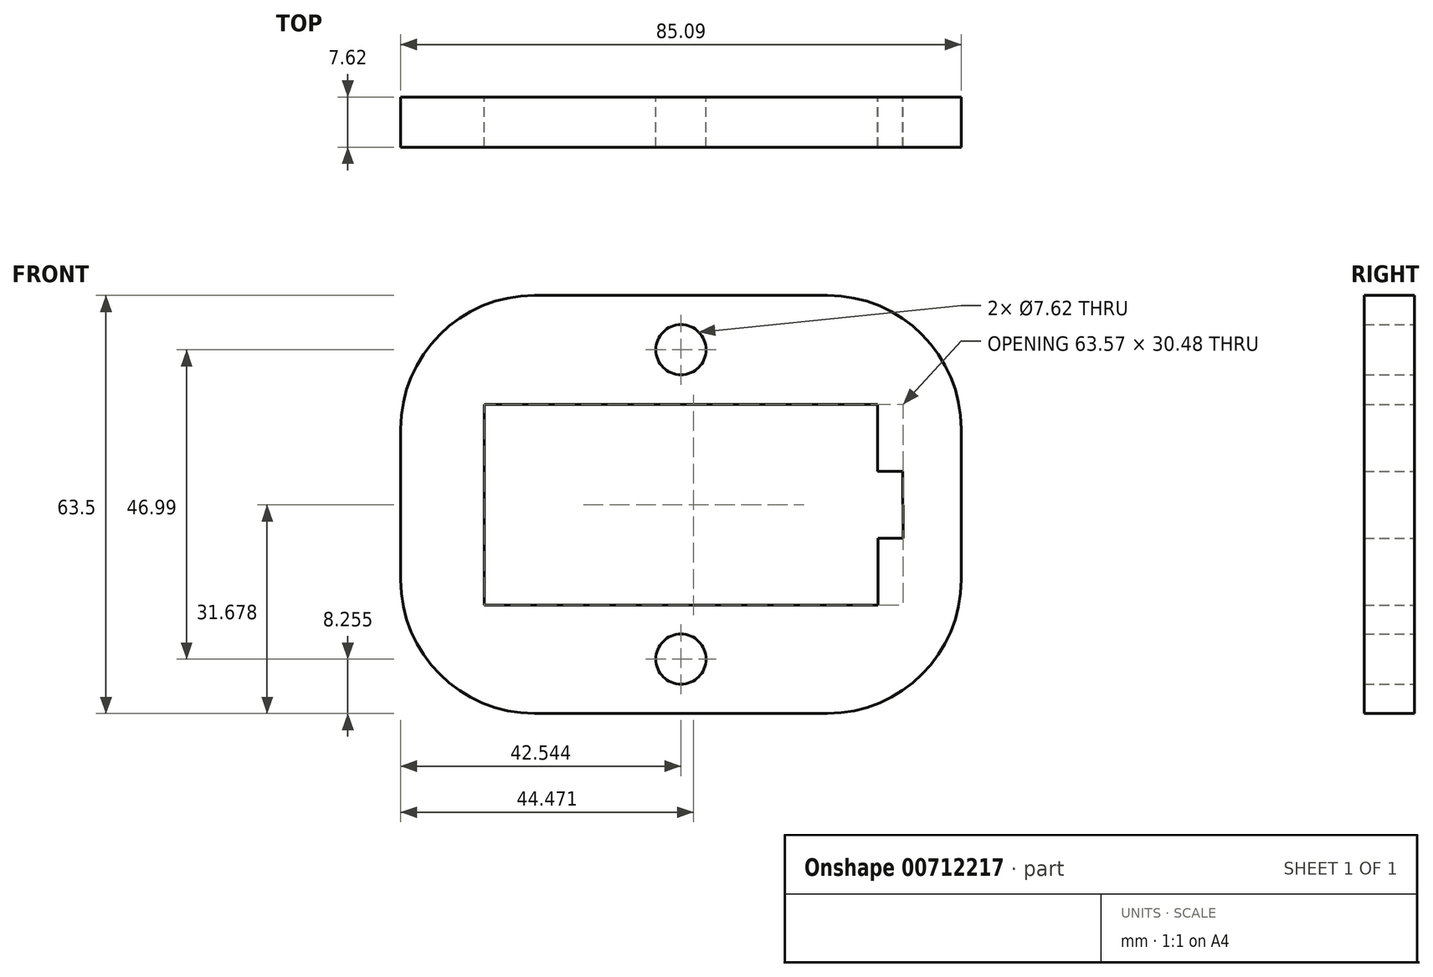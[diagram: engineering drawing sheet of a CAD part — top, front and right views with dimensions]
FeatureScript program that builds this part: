
annotation { "Feature Type Name" : "Feature", "Feature Type Description" : "" }
export const myFeature = defineFeature(function(context is Context, id is Id, definition is map)
    precondition{}
    {
        {
            var Q0;
            Q0=qCreatedBy(makeId("Front.planeOp"),FACE);
            var sketch = newSketch(context, id + "F0", { "sketchPlane" : qUnion([Q0])});
            skLineSegment(sketch, "E0", {"start": v(-66.05, 20.3) * mm, "end": v(19.04, 20.3) * mm});
            skLineSegment(sketch, "E1", {"start": v(19.04, 20.3) * mm, "end": v(19.04, 83.8) * mm});
            skLineSegment(sketch, "E2", {"start": v(19.04, 83.8) * mm, "end": v(-66.05, 83.8) * mm});
            skLineSegment(sketch, "E3", {"start": v(-66.05, 83.8) * mm, "end": v(-66.05, 20.3) * mm});
            skLineSegment(sketch, "E4", {"start": v(-42.14, 36.73) * mm, "end": v(-53.36, 36.73) * mm});
            skLineSegment(sketch, "E5", {"start": v(-42.14, 67.2) * mm, "end": v(-53.36, 67.2) * mm});
            skLineSegment(sketch, "E6", {"start": v(-53.36, 67.2) * mm, "end": v(-53.36, 36.73) * mm});
            skLineSegment(sketch, "E7", {"start": v(-53.36, 36.73) * mm, "end": v(6.34, 36.73) * mm});
            skLineSegment(sketch, "E8", {"start": v(6.34, 67.2) * mm, "end": v(-42.14, 67.2) * mm});
            skCircle(sketch, "E9", {"center": v(-23.5, 75.54) * mm, "radius": 3.81 * mm});
            skCircle(sketch, "E10", {"center": v(-23.5, 28.55) * mm, "radius": 3.81 * mm});
            skLineSegment(sketch, "E11", {"start": v(6.34, 67.2) * mm, "end": v(6.34, 57.05) * mm});
            skLineSegment(sketch, "E12", {"start": v(6.4, 36.74) * mm, "end": v(6.4, 46.9) * mm});
            skLineSegment(sketch, "E13", {"start": v(6.4, 46.9) * mm, "end": v(10.2, 46.9) * mm});
            skLineSegment(sketch, "E14", {"start": v(6.34, 57.05) * mm, "end": v(10.15, 57.05) * mm});
            skLineSegment(sketch, "E15", {"start": v(10.15, 57.05) * mm, "end": v(10.2, 46.9) * mm});
            skLineSegment(sketch, "E16", {"start": v(-53.36, 67.2) * mm, "end": v(6.34, 67.2) * mm});
            skLineSegment(sketch, "E17", {"start": v(10.2, 46.9) * mm, "end": v(6.4, 46.9) * mm});
            skLineSegment(sketch, "E18", {"start": v(6.4, 36.74) * mm, "end": v(-53.36, 36.73) * mm});
            skLineSegment(sketch, "E19", {"start": v(-53.36, 36.73) * mm, "end": v(-53.36, 67.2) * mm});
            skSolve(sketch);
        }
        {
            var Q0;
            Q0=makeQuery(id+"F0.imprint","IMPRINT",FACE,{"disambiguationData":[TD([[makeQuery(id+"F0.imprint","IMPRINT",EDGE,{"derivedFrom":sQuery(id+"F0.wireOp",EDGE,"E0")}),1.0]])]});
            extrude(context, id + "F1", {"entities" : qUnion([Q0]), "depth" : 7.62 * mm, "offsetDistance" : 25.4 * mm});
        }
        {
            var Q0;
            Q0=makeQuery(id+"F1.opExtrude","SWEPT_EDGE",EDGE,{"disambiguationData":[OSD([sQuery(id+"F0.wireOp",EDGE,"E2"),sQuery(id+"F0.wireOp",EDGE,"E3")])]});
            var Q1;
            Q1=makeQuery(id+"F1.opExtrude","SWEPT_EDGE",EDGE,{"disambiguationData":[OSD([sQuery(id+"F0.wireOp",EDGE,"E0"),sQuery(id+"F0.wireOp",EDGE,"E3")])]});
            var Q2;
            Q2=makeQuery(id+"F1.opExtrude","SWEPT_EDGE",EDGE,{"disambiguationData":[OSD([sQuery(id+"F0.wireOp",EDGE,"E0"),sQuery(id+"F0.wireOp",EDGE,"E1")])]});
            var Q3;
            Q3=makeQuery(id+"F1.opExtrude","SWEPT_EDGE",EDGE,{"disambiguationData":[OSD([sQuery(id+"F0.wireOp",EDGE,"E1"),sQuery(id+"F0.wireOp",EDGE,"E2")])]});
            fillet(context, id + "F2", {"entities" : qUnion([Q0, Q1, Q2, Q3]), "radius" : 20.32 * mm, "tangentPropagation" : true, "allowEdgeOverflow" : false});
        }
    });
